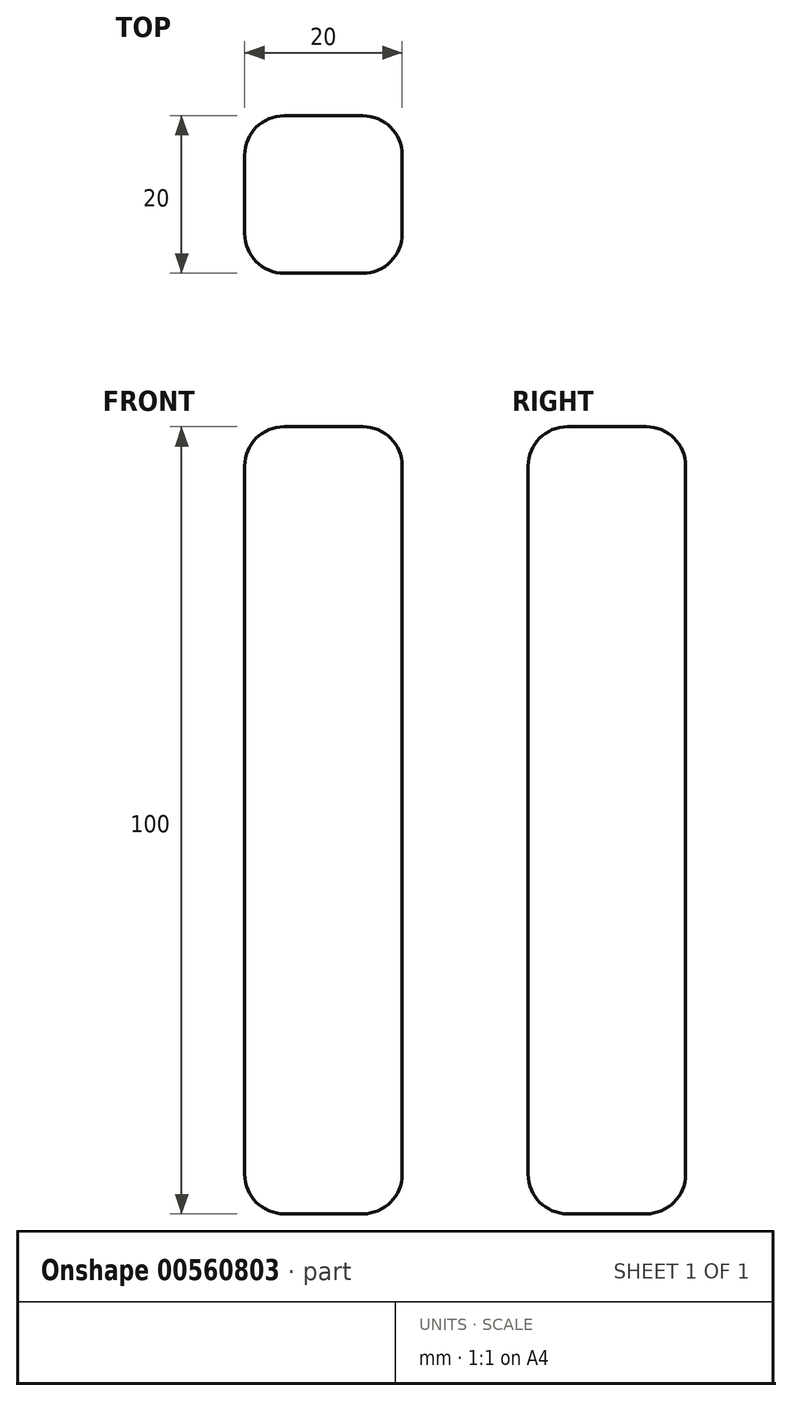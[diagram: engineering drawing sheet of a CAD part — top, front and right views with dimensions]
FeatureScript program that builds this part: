
annotation { "Feature Type Name" : "Feature", "Feature Type Description" : "" }
export const myFeature = defineFeature(function(context is Context, id is Id, definition is map)
    precondition{}
    {
        {
            var Q0;
            Q0=qCreatedBy(makeId("Top.planeOp"),FACE);
            var sketch = newSketch(context, id + "F0", { "sketchPlane" : qUnion([Q0])});
            skLineSegment(sketch, "E0.bottom", {"start": v(-28.07, 4.1) * mm, "end": v(-48.07, 4.1) * mm});
            skLineSegment(sketch, "E0.top", {"start": v(-28.07, 24.1) * mm, "end": v(-48.07, 24.1) * mm});
            skLineSegment(sketch, "E0.left", {"start": v(-28.07, 4.1) * mm, "end": v(-28.07, 24.1) * mm});
            skLineSegment(sketch, "E0.right", {"start": v(-48.07, 4.1) * mm, "end": v(-48.07, 24.1) * mm});
            skSolve(sketch);
        }
        {
            var Q0;
            Q0 = qSketchRegion(id + "F0", true);
            extrude(context, id + "F1", {"entities" : qUnion([Q0]), "depth" : 100 * mm, "offsetDistance" : 25 * mm});
        }
        {
            var Q0;
            Q0=makeQuery(id+"F1.opExtrude","CAP_EDGE",EDGE,{"disambiguationData":[OSD([sQuery(id+"F0.wireOp",EDGE,"E0.top")])],"isStart":false});
            var Q1;
            Q1=makeQuery(id+"F1.opExtrude","CAP_EDGE",EDGE,{"disambiguationData":[OSD([sQuery(id+"F0.wireOp",EDGE,"E0.right")])],"isStart":false});
            var Q2;
            Q2=makeQuery(id+"F1.opExtrude","CAP_EDGE",EDGE,{"disambiguationData":[OSD([sQuery(id+"F0.wireOp",EDGE,"E0.left")])],"isStart":false});
            var Q3;
            Q3=makeQuery(id+"F1.opExtrude","CAP_EDGE",EDGE,{"disambiguationData":[OSD([sQuery(id+"F0.wireOp",EDGE,"E0.bottom")])],"isStart":false});
            var Q4;
            Q4=makeQuery(id+"F1.opExtrude","SWEPT_EDGE",EDGE,{"disambiguationData":[OSD([sQuery(id+"F0.wireOp",EDGE,"E0.top"),sQuery(id+"F0.wireOp",EDGE,"E0.right")])]});
            var Q5;
            Q5=makeQuery(id+"F1.opExtrude","SWEPT_EDGE",EDGE,{"disambiguationData":[OSD([sQuery(id+"F0.wireOp",EDGE,"E0.bottom"),sQuery(id+"F0.wireOp",EDGE,"E0.right")])]});
            var Q6;
            Q6=makeQuery(id+"F1.opExtrude","SWEPT_EDGE",EDGE,{"disambiguationData":[OSD([sQuery(id+"F0.wireOp",EDGE,"E0.bottom"),sQuery(id+"F0.wireOp",EDGE,"E0.left")])]});
            var Q7;
            Q7=makeQuery(id+"F1.opExtrude","CAP_EDGE",EDGE,{"disambiguationData":[OSD([sQuery(id+"F0.wireOp",EDGE,"E0.left")])],"isStart":true});
            var Q8;
            Q8=makeQuery(id+"F1.opExtrude","SWEPT_FACE",FACE,{"disambiguationData":[OSD([sQuery(id+"F0.wireOp",EDGE,"E0.left")])]});
            var Q9;
            Q9=makeQuery(id+"F1.opExtrude","CAP_FACE",FACE,{"disambiguationData":[OSD([sQuery(id+"F0.wireOp",EDGE,"E0.bottom"),sQuery(id+"F0.wireOp",EDGE,"E0.top"),sQuery(id+"F0.wireOp",EDGE,"E0.left"),sQuery(id+"F0.wireOp",EDGE,"E0.right")])],"isStart":true});
            fillet(context, id + "F2", {"entities" : qUnion([Q0, Q1, Q2, Q3, Q4, Q5, Q6, Q7, Q8, Q9]), "radius" : 5 * mm, "tangentPropagation" : true, "allowEdgeOverflow" : false});
        }
    });
